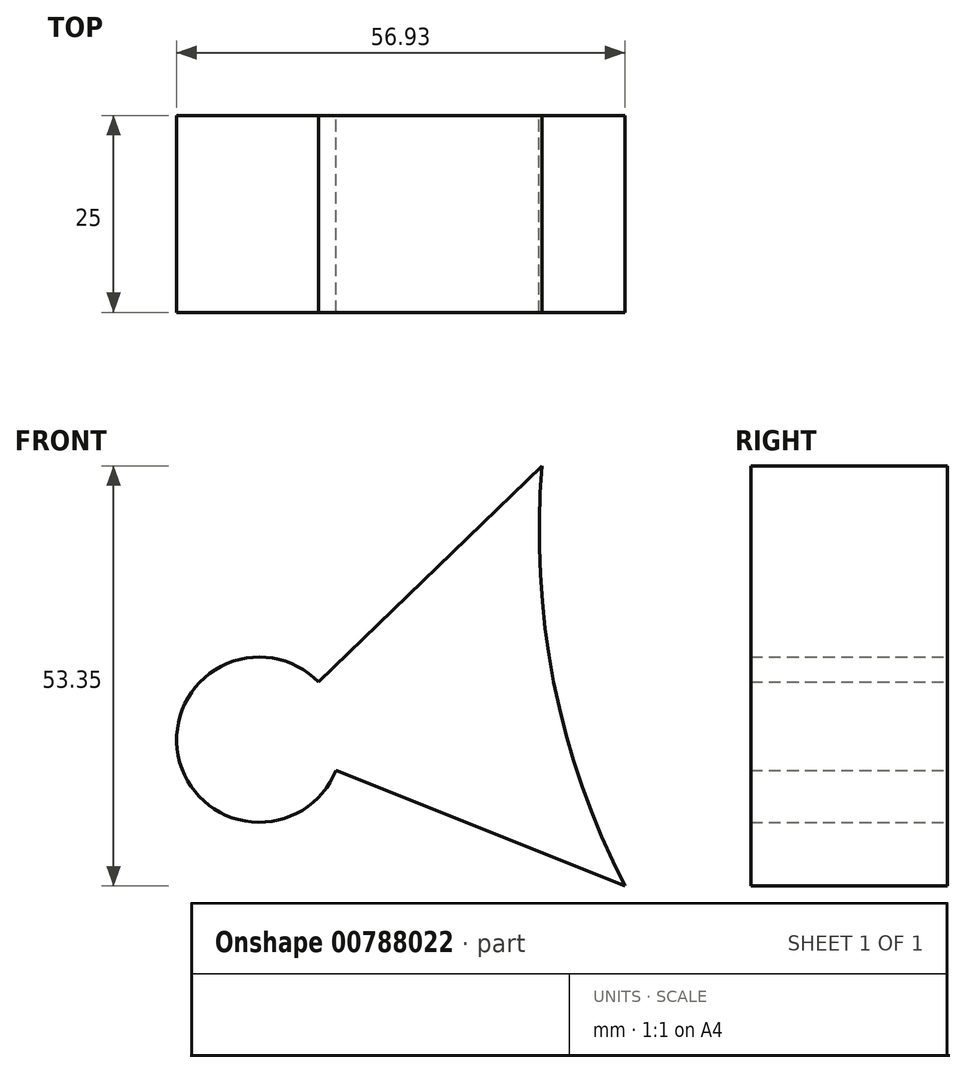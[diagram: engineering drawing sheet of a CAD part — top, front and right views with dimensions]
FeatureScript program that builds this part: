
annotation { "Feature Type Name" : "Feature", "Feature Type Description" : "" }
export const myFeature = defineFeature(function(context is Context, id is Id, definition is map)
    precondition{}
    {
        {
            var Q0;
            Q0=qCreatedBy(makeId("Front.planeOp"),FACE);
            var sketch = newSketch(context, id + "F0", { "sketchPlane" : qUnion([Q0])});
            skCircle(sketch, "E0", {"center": v(-23.46, -14.25) * mm, "radius": 10.5 * mm});
            skLineSegment(sketch, "E1", {"start": v(-23.46, -14.25) * mm, "end": v(12.46, 20.53) * mm});
            skLineSegment(sketch, "E2", {"start": v(-23.46, -14.25) * mm, "end": v(22.97, -32.82) * mm});
            skLineSegment(sketch, "E3", {"start": v(12.46, 20.53) * mm, "end": v(-23.46, -14.25) * mm});
            skArc(sketch, "E4", {"start": v(12.46, 20.53) * mm, "mid": v(13.94, -6.88) * mm, "end": v(22.97, -32.82) * mm});
            skSolve(sketch);
        }
        {
            var Q0;
            Q0 = qSketchRegion(id + "F0", true);
            extrude(context, id + "F1", {"entities" : qUnion([Q0]), "depth" : 25 * mm, "offsetDistance" : 25 * mm});
        }
    });
